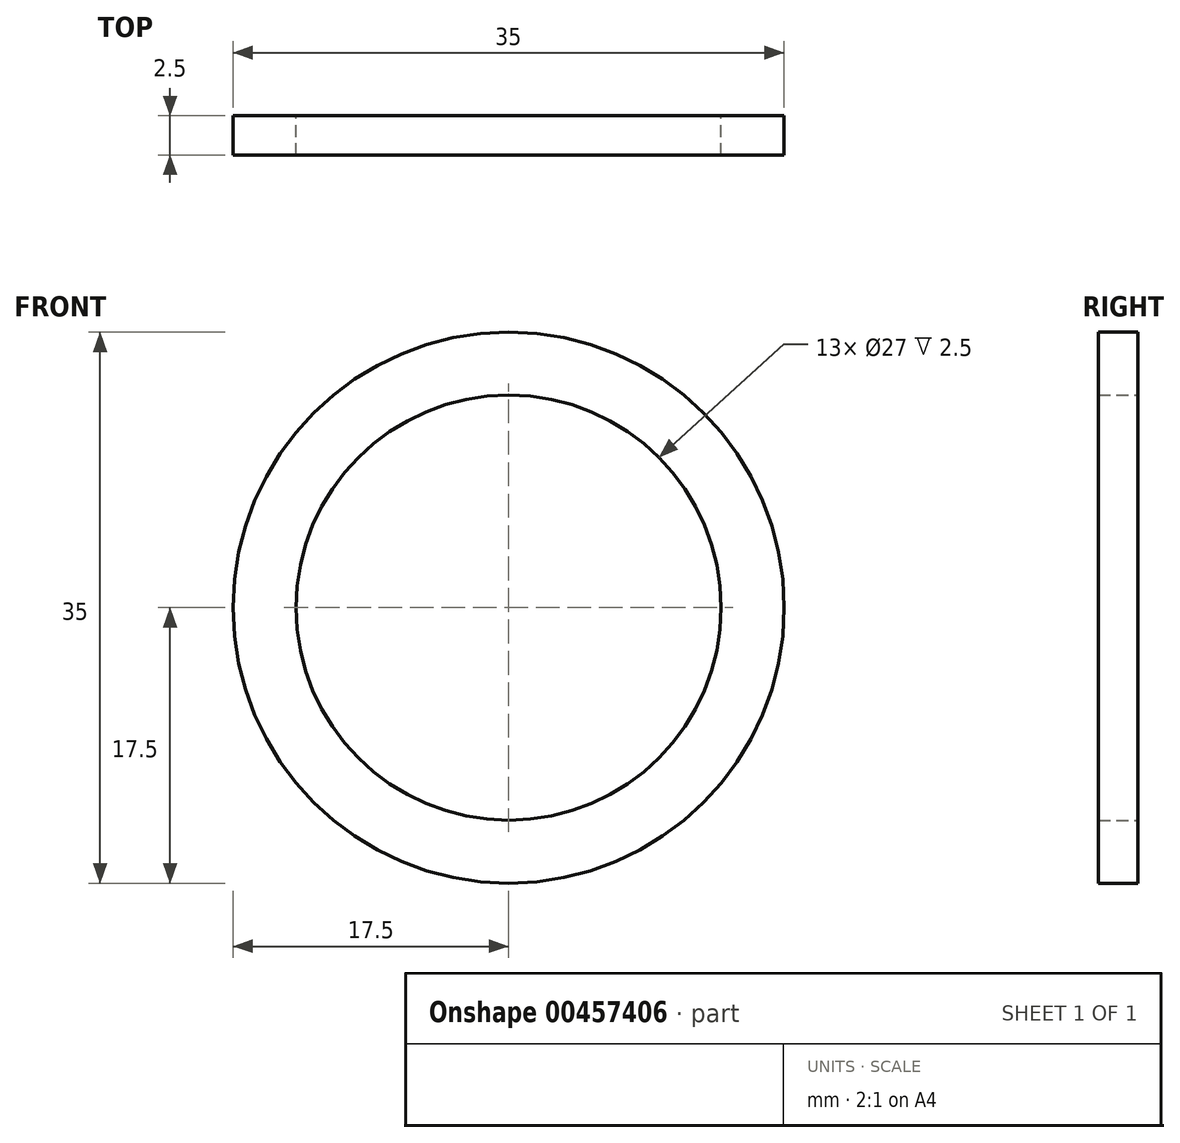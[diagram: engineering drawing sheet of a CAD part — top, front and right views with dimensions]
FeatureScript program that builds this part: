
annotation { "Feature Type Name" : "Feature", "Feature Type Description" : "" }
export const myFeature = defineFeature(function(context is Context, id is Id, definition is map)
    precondition{}
    {
        {
            var Q0;
            Q0=qCreatedBy(makeId("Front.planeOp"),FACE);
            var sketch = newSketch(context, id + "F0", { "sketchPlane" : qUnion([Q0])});
            skCircle(sketch, "E0", {"center": v(0, 0) * mm, "radius": 17.5 * mm});
            skCircle(sketch, "E1", {"center": v(0, 0) * mm, "radius": 13.5 * mm});
            skSolve(sketch);
        }
        {
            var Q0;
            Q0=makeQuery(id+"F0.imprint","IMPRINT",FACE,{"disambiguationData":[TD([[makeQuery(id+"F0.imprint","IMPRINT",EDGE,{"derivedFrom":sQuery(id+"F0.wireOp",EDGE,"E0")}),1.0]])]});
            extrude(context, id + "F1", {"entities" : qUnion([Q0]), "depth" : 2.5 * mm});
        }
    });
